# Revit family: RESERVOIR D'AIR
name_source: partatom
category: Equipement de génie climatique
revit_build: Autodesk Revit 2018 (Build: 20170223_1515(x64)
units: mm (PartAtom-declared; Revit-internal decimal feet)

## family parameters
Basée sur le plan de construction = Non
Classification = Aucun
Cote de connecteur circulaire = Utiliser le diamètre
Couper avec des vides une fois chargée = Non
Partagée = Non
Point de calcul de pièce = Non
Toujours verticalement = Oui
Type d'élément = Normal

## types (10) — shared parameters
BRANCHEMENT_TERRE = Oui
DESCRIPTION_PURGE = G1/2"
DIAM_PURGE = 15 mm  [stored 0.0492126 ft]
EP_BOUCH = 6.3 mm
EP_PATTE = 3 mm  [stored 0.00984252 ft]
Fabricant = MIL'S
HAUT_LEVAGE = 52.4 mm
HAUT_VIROLE_PIED = 220 mm  [stored 0.721785 ft]
LARG_PATTE = 40 mm  [stored 0.131234 ft]
LONG_BOSS = 25 mm  [stored 0.082021 ft]
LONG_BOUCH = 19 mm  [stored 0.062336 ft]
LONG_OUVERTURE = 255 mm
RAYON_PATTE = 375 mm
ØBOSS_BAS = 26.5 mm  [stored 0.0869423 ft]
ØPATTE = 750 mm
ØVIROLE_BAS = 1105 mm
ØVIROLE_BAS_INT = 1099 mm

## per-type parameters (varying)
- AIR-11B-500L: DESCR_ASPI=ENTREE RESERVOIR ; G1"; DESCR_REFOUL=SORTIE RESERVOIR ; G1"; DESCR_RESERV=RESERVOIR AIR ; 11Bar ; 500L; DIAMETRE=600 mm; DIAM_ASPI_AIR=25 mm  [stored 0.082021 ft]; DIAM_REFOUL_AIR=25 mm  [stored 0.082021 ft]; HAUTEUR=2091 mm; HAUT_FOND=189 mm  [stored 0.620079 ft]; LONG_BOSS_BAS=15 mm  [stored 0.0492126 ft]; LONG_VIROLE=1500 mm; OFFSET_BOSS=313 mm; OFFSET_BOSS_BAS=173 mm  [stored 0.567585 ft]; OFFSET_HAUT_BOSS_1=785 mm; OFFSET_HAUT_BOSS_2=1655 mm; OFFSET_HAUT_BOSS_3=1655 mm; OFFSET_HAUT_FOND=188 mm  [stored 0.616798 ft]; OFFSET_PATTE_EXT=291 mm; OFFSET_PATTE_INT=201 mm  [stored 0.659449 ft]; POIDS(Kg)=128 mm  [stored 0.419948 ft]; RAY_BOUCH=33 mm  [stored 0.108268 ft]; RAY_PAN_BOUCH=15 mm  [stored 0.0492126 ft]; TAILLE_VANNE=Vanne BS FF : DN25 - G1" - FF (231 0001); TYPE_PIED=PIEDS RESERVOIR AIR : AIR-11B-500L; ØBOSS=66 mm  [stored 0.216535 ft]; ØBOSS_2=17.5 mm  [stored 0.0574147 ft]; ØVIROLE=600 mm
- AIR-11B-900L: DESCR_ASPI=ENTREE RESERVOIR ; G1"; DESCR_REFOUL=SORTIE RESERVOIR ; G1"; DESCR_RESERV=RESERVOIR AIR ; 11Bar ; 900L; DIAMETRE=795 mm; DIAM_ASPI_AIR=25 mm  [stored 0.082021 ft]; DIAM_REFOUL_AIR=25 mm  [stored 0.082021 ft]; HAUTEUR=2150 mm; HAUT_FOND=230 mm; LONG_BOSS_BAS=15 mm  [stored 0.0492126 ft]; LONG_VIROLE=1500 mm; OFFSET_BOSS=430 mm; OFFSET_BOSS_BAS=145 mm  [stored 0.475722 ft]; OFFSET_HAUT_BOSS_1=785 mm; OFFSET_HAUT_BOSS_2=1655 mm; OFFSET_HAUT_BOSS_3=1655 mm; OFFSET_HAUT_FOND=160 mm  [stored 0.524934 ft]; OFFSET_PATTE_EXT=398 mm; OFFSET_PATTE_INT=330 mm; POIDS(Kg)=215 mm; RAY_BOUCH=33 mm  [stored 0.108268 ft]; RAY_PAN_BOUCH=15 mm  [stored 0.0492126 ft]; TAILLE_VANNE=Vanne BS FF : DN25 - G1" - FF (231 0001); TYPE_PIED=PIEDS RESERVOIR AIR : AIR-11B-500L; ØBOSS=66 mm  [stored 0.216535 ft]; ØBOSS_2=17.5 mm  [stored 0.0574147 ft]; ØVIROLE=795 mm
- AIR-12B-1000L: DESCR_ASPI=ENTREE RESERVOIR ; G1_1/4"; DESCR_REFOUL=SORTIE RESERVOIR ; G1_1/4"; DESCR_RESERV=RESERVOIR AIR ; 12Bar ; 1000L; DIAMETRE=800 mm; DIAM_ASPI_AIR=32 mm  [stored 0.104987 ft]; DIAM_REFOUL_AIR=32 mm  [stored 0.104987 ft]; HAUTEUR=2360 mm; HAUT_FOND=210 mm  [stored 0.688976 ft]; LONG_BOSS_BAS=20 mm  [stored 0.0656168 ft]; LONG_VIROLE=1700 mm; OFFSET_BOSS=430 mm; OFFSET_BOSS_BAS=183 mm; OFFSET_HAUT_BOSS_1=740 mm; OFFSET_HAUT_BOSS_2=1680 mm; OFFSET_HAUT_BOSS_3=1680 mm; OFFSET_HAUT_FOND=203 mm  [stored 0.66601 ft]; OFFSET_PATTE_EXT=398 mm; OFFSET_PATTE_INT=330 mm; POIDS(Kg)=260 mm; RAY_BOUCH=33 mm  [stored 0.108268 ft]; RAY_PAN_BOUCH=15 mm  [stored 0.0492126 ft]; TAILLE_VANNE=Vanne BS FF : DN32 - G1"1/4 - FF (231 0005); TYPE_PIED=PIEDS RESERVOIR AIR : AIR-11B-500L; ØBOSS=66 mm  [stored 0.216535 ft]; ØBOSS_2=17.5 mm  [stored 0.0574147 ft]; ØVIROLE=800 mm
- AIR-15B-1000L: DESCR_ASPI=ENTREE RESERVOIR ; G1_1/4"; DESCR_REFOUL=SORTIE RESERVOIR ; G1_1/4"; DESCR_RESERV=RESERVOIR AIR ; 15Bar ; 1000L; DIAMETRE=800 mm; DIAM_ASPI_AIR=32 mm  [stored 0.104987 ft]; DIAM_REFOUL_AIR=32 mm  [stored 0.104987 ft]; HAUTEUR=2360 mm; HAUT_FOND=230 mm; LONG_BOSS_BAS=20 mm  [stored 0.0656168 ft]; LONG_VIROLE=1700 mm; OFFSET_BOSS=417 mm; OFFSET_BOSS_BAS=150 mm; OFFSET_HAUT_BOSS_1=760 mm; OFFSET_HAUT_BOSS_2=1700 mm; OFFSET_HAUT_BOSS_3=1700 mm; OFFSET_HAUT_FOND=170 mm  [stored 0.557743 ft]; OFFSET_PATTE_EXT=398 mm; OFFSET_PATTE_INT=330 mm; POIDS(Kg)=272 mm; RAY_BOUCH=33 mm  [stored 0.108268 ft]; RAY_PAN_BOUCH=15 mm  [stored 0.0492126 ft]; TAILLE_VANNE=Vanne BS FF : DN32 - G1"1/4 - FF (231 0005); TYPE_PIED=PIEDS RESERVOIR AIR : AIR-11B-500L; ØBOSS=66 mm  [stored 0.216535 ft]; ØBOSS_2=17.5 mm  [stored 0.0574147 ft]; ØVIROLE=800 mm
- AIR-12B-1500L: DESCR_ASPI=ENTREE RESERVOIR ; G1_1/4"; DESCR_REFOUL=SORTIE RESERVOIR ; G1_1/4"; DESCR_RESERV=RESERVOIR AIR ; 12Bar ; 1500L; DIAMETRE=1000 mm; DIAM_ASPI_AIR=32 mm  [stored 0.104987 ft]; DIAM_REFOUL_AIR=32 mm  [stored 0.104987 ft]; HAUTEUR=2315 mm; HAUT_FOND=300 mm; LONG_BOSS_BAS=15 mm  [stored 0.0492126 ft]; LONG_VIROLE=1500 mm; OFFSET_BOSS=517 mm; OFFSET_BOSS_BAS=170 mm  [stored 0.557743 ft]; OFFSET_HAUT_BOSS_1=1780 mm; OFFSET_HAUT_BOSS_2=680 mm; OFFSET_HAUT_BOSS_3=1780 mm; OFFSET_HAUT_FOND=185 mm  [stored 0.606955 ft]; OFFSET_PATTE_EXT=398 mm; OFFSET_PATTE_INT=330 mm; POIDS(Kg)=311 mm; RAY_BOUCH=33 mm  [stored 0.108268 ft]; RAY_PAN_BOUCH=15 mm  [stored 0.0492126 ft]; TAILLE_VANNE=Vanne BS FF : DN32 - G1"1/4 - FF (231 0005); TYPE_PIED=PIEDS RESERVOIR AIR : AIR-11B-500L; ØBOSS=66 mm  [stored 0.216535 ft]; ØBOSS_2=20 mm  [stored 0.0656168 ft]; ØVIROLE=1000 mm
- AIR-15B-1500L: DESCR_ASPI=ENTREE RESERVOIR ; G1_1/4"; DESCR_REFOUL=SORTIE RESERVOIR ; G1_1/4"; DESCR_RESERV=RESERVOIR AIR ; 15Bar ; 1500L; DIAMETRE=1000 mm; DIAM_ASPI_AIR=32 mm  [stored 0.104987 ft]; DIAM_REFOUL_AIR=32 mm  [stored 0.104987 ft]; HAUTEUR=2315 mm; HAUT_FOND=295 mm; LONG_BOSS_BAS=20 mm  [stored 0.0656168 ft]; LONG_VIROLE=1500 mm; OFFSET_BOSS=517 mm; OFFSET_BOSS_BAS=170 mm  [stored 0.557743 ft]; OFFSET_HAUT_BOSS_1=1780 mm; OFFSET_HAUT_BOSS_2=680 mm; OFFSET_HAUT_BOSS_3=1780 mm; OFFSET_HAUT_FOND=190 mm; OFFSET_PATTE_EXT=398 mm; OFFSET_PATTE_INT=330 mm; POIDS(Kg)=284 mm; RAY_BOUCH=33 mm  [stored 0.108268 ft]; RAY_PAN_BOUCH=15 mm  [stored 0.0492126 ft]; TAILLE_VANNE=Vanne BS FF : DN32 - G1"1/4 - FF (231 0005); TYPE_PIED=PIEDS RESERVOIR AIR : AIR-11B-500L; ØBOSS=66 mm  [stored 0.216535 ft]; ØBOSS_2=20 mm  [stored 0.0656168 ft]; ØVIROLE=1000 mm
- AIR-12B-2000L: DESCR_ASPI=ENTREE RESERVOIR ; G1_1/4"; DESCR_REFOUL=SORTIE RESERVOIR ; G1_1/4"; DESCR_RESERV=RESERVOIR AIR ; 12Bar ; 2000L; DIAMETRE=1100 mm; DIAM_ASPI_AIR=32 mm  [stored 0.104987 ft]; DIAM_REFOUL_AIR=32 mm  [stored 0.104987 ft]; HAUTEUR=2500 mm; HAUT_FOND=300 mm; LONG_BOSS_BAS=20 mm  [stored 0.0656168 ft]; LONG_VIROLE=1650 mm; OFFSET_BOSS=567 mm; OFFSET_BOSS_BAS=200 mm  [stored 0.656168 ft]; OFFSET_HAUT_BOSS_1=1970 mm; OFFSET_HAUT_BOSS_2=770 mm; OFFSET_HAUT_BOSS_3=1755 mm; OFFSET_HAUT_FOND=220 mm  [stored 0.721785 ft]; OFFSET_PATTE_EXT=398 mm; OFFSET_PATTE_INT=330 mm; POIDS(Kg)=360 mm; RAY_BOUCH=33 mm  [stored 0.108268 ft]; RAY_PAN_BOUCH=15 mm  [stored 0.0492126 ft]; TAILLE_VANNE=Vanne BS FF : DN32 - G1"1/4 - FF (231 0005); TYPE_PIED=PIEDS RESERVOIR AIR : AIR-12B-2000L; ØBOSS=66 mm  [stored 0.216535 ft]; ØBOSS_2=20 mm  [stored 0.0656168 ft]; ØVIROLE=1100 mm
- AIR-15B-2000L: DESCR_ASPI=ENTREE RESERVOIR ; G1_1/4"; DESCR_REFOUL=SORTIE RESERVOIR ; G1_1/4"; DESCR_RESERV=RESERVOIR AIR ; 15Bar ; 2000L; DIAMETRE=1000 mm; DIAM_ASPI_AIR=32 mm  [stored 0.104987 ft]; DIAM_REFOUL_AIR=32 mm  [stored 0.104987 ft]; HAUTEUR=2760 mm; HAUT_FOND=295 mm; LONG_BOSS_BAS=20 mm  [stored 0.0656168 ft]; LONG_VIROLE=1950 mm; OFFSET_BOSS=517 mm; OFFSET_BOSS_BAS=170 mm  [stored 0.557743 ft]; OFFSET_HAUT_BOSS_1=2210 mm; OFFSET_HAUT_BOSS_2=880 mm; OFFSET_HAUT_BOSS_3=2210 mm; OFFSET_HAUT_FOND=190 mm; OFFSET_PATTE_EXT=398 mm; OFFSET_PATTE_INT=330 mm; POIDS(Kg)=490 mm; RAY_BOUCH=33 mm  [stored 0.108268 ft]; RAY_PAN_BOUCH=15 mm  [stored 0.0492126 ft]; TAILLE_VANNE=Vanne BS FF : DN32 - G1"1/4 - FF (231 0005); TYPE_PIED=PIEDS RESERVOIR AIR : AIR-15B-2000L; ØBOSS=66 mm  [stored 0.216535 ft]; ØBOSS_2=20 mm  [stored 0.0656168 ft]; ØVIROLE=1000 mm
- AIR-15B-500L: DESCR_ASPI=ENTREE RESERVOIR ; G1_1/4"; DESCR_REFOUL=SORTIE RESERVOIR ; G1_1/4"; DESCR_RESERV=RESERVOIR AIR ; 15Bar ; 500L; DIAMETRE=600 mm; DIAM_ASPI_AIR=32 mm  [stored 0.104987 ft]; DIAM_REFOUL_AIR=32 mm  [stored 0.104987 ft]; HAUTEUR=2065 mm; HAUT_FOND=181 mm  [stored 0.593832 ft]; LONG_BOSS_BAS=16 mm  [stored 0.0524934 ft]; LONG_VIROLE=1500 mm; Lien espace client=https://www.mils.fr; Modèle=Réservoir d'air vertical; OFFSET_BOSS=313 mm; OFFSET_BOSS_BAS=161 mm  [stored 0.528215 ft]; OFFSET_HAUT_BOSS_1=785 mm; OFFSET_HAUT_BOSS_2=1655 mm; OFFSET_HAUT_BOSS_3=1655 mm; OFFSET_HAUT_FOND=176 mm  [stored 0.577428 ft]; OFFSET_PATTE_EXT=291 mm; OFFSET_PATTE_INT=201 mm  [stored 0.659449 ft]; POIDS(Kg)=164 mm  [stored 0.538058 ft]; RAY_BOUCH=33 mm  [stored 0.108268 ft]; RAY_PAN_BOUCH=15 mm  [stored 0.0492126 ft]; TAILLE_VANNE=Vanne BS FF : DN32 - G1"1/4 - FF (231 0005); TYPE_PIED=PIEDS RESERVOIR AIR : AIR-11B-500L; ØBOSS=66 mm  [stored 0.216535 ft]; ØBOSS_2=17.5 mm  [stored 0.0574147 ft]; ØVIROLE=600 mm
- AIR-11B-270L: DESCR_ASPI=ENTREE RESERVOIR ; G1"; DESCR_REFOUL=SORTIE RESERVOIR ; G1"; DESCR_RESERV=RESERVOIR AIR ; 11Bar ; 270L; DIAMETRE=600 mm; DIAM_ASPI_AIR=25 mm  [stored 0.082021 ft]; DIAM_REFOUL_AIR=25 mm  [stored 0.082021 ft]; HAUTEUR=1655 mm; HAUT_FOND=154 mm  [stored 0.505249 ft]; LONG_BOSS_BAS=15 mm  [stored 0.0492126 ft]; LONG_VIROLE=1150 mm; OFFSET_BOSS=313 mm; OFFSET_BOSS_BAS=157 mm  [stored 0.515092 ft]; OFFSET_HAUT_BOSS_1=600 mm; OFFSET_HAUT_BOSS_2=1305 mm; OFFSET_HAUT_BOSS_3=1305 mm; OFFSET_HAUT_FOND=172 mm  [stored 0.564304 ft]; OFFSET_PATTE_EXT=291 mm; OFFSET_PATTE_INT=201 mm  [stored 0.659449 ft]; POIDS(Kg)=63 mm  [stored 0.206693 ft]; RAY_BOUCH=20 mm  [stored 0.0656168 ft]; RAY_PAN_BOUCH=10 mm  [stored 0.0328084 ft]; TAILLE_VANNE=Vanne BS FF : DN25 - G1" - FF (231 0001); TYPE_PIED=PIEDS RESERVOIR AIR : AIR-11B-270L; ØBOSS=40 mm  [stored 0.131234 ft]; ØBOSS_2=17.5 mm  [stored 0.0574147 ft]; ØVIROLE=600 mm

note: [stored X ft] marks values corroborated as IEEE doubles in the binary element streams (Revit-internal decimal feet)

## geometry (parser evidence)
native form markers: Sweep x7
no freeform markers — native parametric forms only
